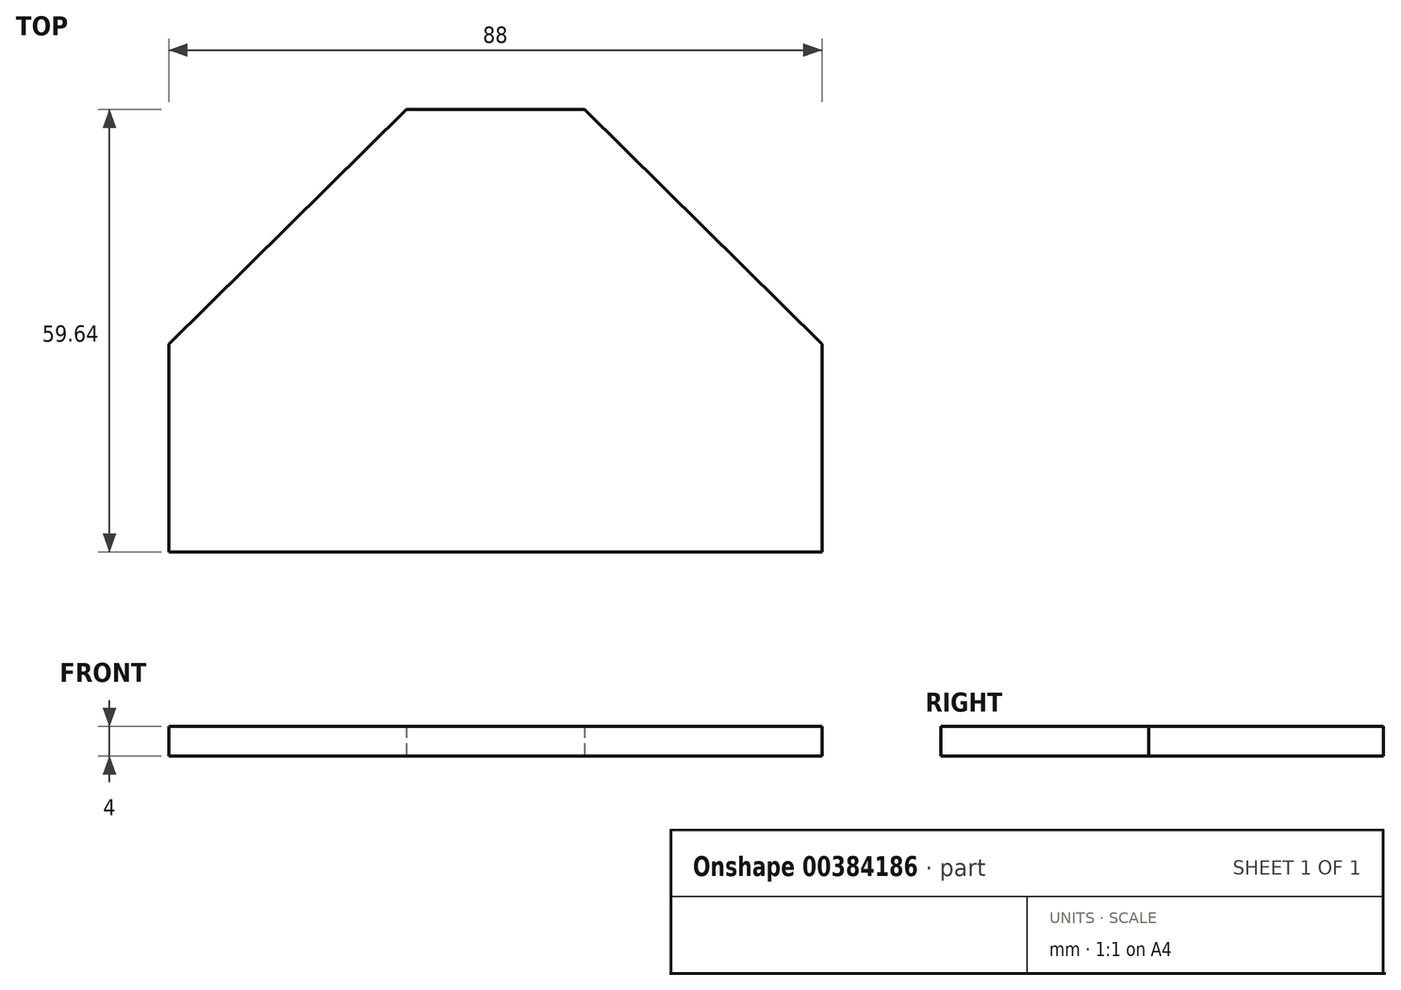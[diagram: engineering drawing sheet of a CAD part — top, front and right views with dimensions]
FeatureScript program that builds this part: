
annotation { "Feature Type Name" : "Feature", "Feature Type Description" : "" }
export const myFeature = defineFeature(function(context is Context, id is Id, definition is map)
    precondition{}
    {
        {
            var Q0;
            Q0=qCreatedBy(makeId("Top.planeOp"),FACE);
            var sketch = newSketch(context, id + "F0", { "sketchPlane" : qUnion([Q0])});
            skLineSegment(sketch, "E0", {"start": v(44, 0.36) * mm, "end": v(44, 28.36) * mm});
            skLineSegment(sketch, "E1", {"start": v(12, 60) * mm, "end": v(44, 28.36) * mm});
            skLineSegment(sketch, "E2", {"start": v(12, 60) * mm, "end": v(-12, 60) * mm});
            skLineSegment(sketch, "E3", {"start": v(44, 0.36) * mm, "end": v(-44, 0.36) * mm});
            skLineSegment(sketch, "E4", {"start": v(-44, 0.36) * mm, "end": v(-44, 28.36) * mm});
            skLineSegment(sketch, "E5", {"start": v(-12, 60) * mm, "end": v(-44, 28.36) * mm});
            skSolve(sketch);
        }
        {
            var Q0;
            Q0 = qSketchRegion(id + "F0", true);
            extrude(context, id + "F1", {"entities" : qUnion([Q0]), "depth" : 4 * mm});
        }
    });
